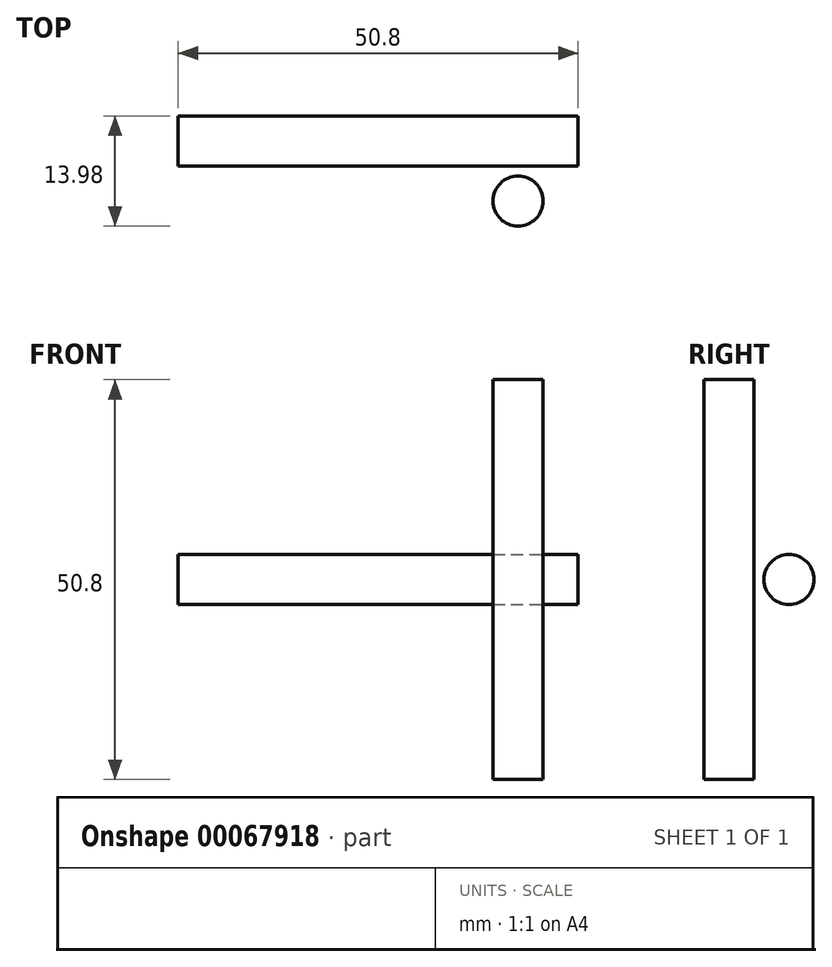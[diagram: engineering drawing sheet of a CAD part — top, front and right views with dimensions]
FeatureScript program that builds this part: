
annotation { "Feature Type Name" : "Feature", "Feature Type Description" : "" }
export const myFeature = defineFeature(function(context is Context, id is Id, definition is map)
    precondition{}
    {
        {
            assignVariable(context, id + "F0", {"name" : "ZPos", "anyValue" : 2});
        }
        {
            var Q0;
            Q0=qCreatedBy(makeId("Top.planeOp"),FACE);
            var sketch = newSketch(context, id + "F1", { "sketchPlane" : qUnion([Q0])});
            skCircle(sketch, "E0.cCircle", {"center": v(0, 0) * mm, "radius": 152.4 * mm, "construction": true});
            skLineSegment(sketch, "E0.0", {"start": v(87.99, 152.4) * mm, "end": v(175.98, 0) * mm});
            skLineSegment(sketch, "E0.1", {"start": v(175.98, 0) * mm, "end": v(87.99, -152.4) * mm});
            skLineSegment(sketch, "E0.2", {"start": v(87.99, -152.4) * mm, "end": v(-87.99, -152.4) * mm});
            skLineSegment(sketch, "E0.3", {"start": v(-87.99, -152.4) * mm, "end": v(-175.98, 0) * mm});
            skLineSegment(sketch, "E0.4", {"start": v(-175.98, 0) * mm, "end": v(-87.99, 152.4) * mm});
            skLineSegment(sketch, "E0.5", {"start": v(-87.99, 152.4) * mm, "end": v(87.99, 152.4) * mm});
            skPoint(sketch, "E0.0.midPoint", {"position": v(131.98, 76.2) * mm});
            skText(sketch, "E1", { "text": "1\n", "fontName": "OpenSans-Regular.ttf"});
            skText(sketch, "E2", { "text": "2\n", "fontName": "OpenSans-Regular.ttf"});
            skText(sketch, "E3", { "text": "3\n", "fontName": "OpenSans-Regular.ttf"});
            const initialGuessF1  = {"E1": [-0.00997, -0.1984, 1, 0, 0.02637], "E2": [0.15081, 0.07402, 1, 0, 0.02748], "E3": [-0.18048, 0.09683, 1, 0, 0.028]};
            skSetInitialGuess(sketch, initialGuessF1);
            skSolve(sketch);
        }
        {
            var Q0;
            Q0=makeQuery(id+"F1.imprint","IMPRINT",FACE,{"disambiguationData":[TD([[makeQuery(id+"F1.imprint","IMPRINT",EDGE,{"derivedFrom":sQuery(id+"F1.wireOp",EDGE,"E0.0")}),-1.0]])]});
            cPlane(context, id + "F2", {"entities" : qUnion([Q0]), "cplaneType" : CPlaneType.OFFSET, "offset" : (getVariable(context, 'ZPos')) * mm, "width" : 152.4 * mm, "height" : 152.4 * mm});
        }
        {
            var Q0;
            Q0=qCreatedBy(id+"F2.planeOp",FACE);
            var sketch = newSketch(context, id + "F3", { "sketchPlane" : qUnion([Q0])});
            skCircle(sketch, "E4.cCircle", {"center": v(-127, 127) * mm, "radius": 14.66 * mm, "construction": true});
            skLineSegment(sketch, "E4.0", {"start": v(-127, 156.33) * mm, "end": v(-101.6, 112.34) * mm});
            skLineSegment(sketch, "E4.1", {"start": v(-101.6, 112.34) * mm, "end": v(-152.4, 112.34) * mm});
            skLineSegment(sketch, "E4.2", {"start": v(-152.4, 112.34) * mm, "end": v(-127, 156.33) * mm});
            skPoint(sketch, "E4.0.midPoint", {"position": v(-114.3, 134.33) * mm});
            skSolve(sketch);
        }
        {
            var Q0;
            Q0=makeQuery(id+"F1.imprint","IMPRINT",FACE,{"disambiguationData":[TD([[makeQuery(id+"F1.imprint","IMPRINT",EDGE,{"derivedFrom":sQuery(id+"F1.wireOp",EDGE,"E0.0")}),-1.0]])]});
            var sketch = newSketch(context, id + "F4", { "sketchPlane" : qUnion([Q0])});
            skLineSegment(sketch, "E5", {"start": v(-25.4, -139.7) * mm, "end": v(25.4, -139.7) * mm});
            skLineSegment(sketch, "E6.1.0", {"start": v(133.68, 47.85) * mm, "end": v(108.28, 91.85) * mm});
            skLineSegment(sketch, "E6.2.0", {"start": v(-108.28, 91.85) * mm, "end": v(-133.68, 47.85) * mm});
            skPoint(sketch, "E6.center", {"position": v(0, 0) * mm});
            skSolve(sketch);
        }
        {
            var Q0;
            Q0=sQuery(id+"F3.wireOp",VERTEX,"E4.2.start");
            var Q1;
            Q1=sQuery(id+"F4.wireOp",VERTEX,"E5.start");
            var Q2;
            Q2=sQuery(id+"F4.wireOp",VERTEX,"E5.end");
            cPlane(context, id + "F5", {"entities" : qUnion([Q0, Q1, Q2]), "cplaneType" : CPlaneType.THREE_POINT, "offset" : 0 * mm, "width" : 152.4 * mm, "height" : 152.4 * mm});
        }
        {
            var Q0;
            Q0=qCreatedBy(id+"F5.planeOp",FACE);
            var sketch = newSketch(context, id + "F6", { "sketchPlane" : qUnion([Q0])});
            skLineSegment(sketch, "E7.0", {"start": v(-25.4, 136.95) * mm, "end": v(25.4, 136.95) * mm});
            skCircle(sketch, "E8", {"center": v(20.52, 132.07) * mm, "radius": 4.87 * mm});
            skLineSegment(sketch, "E9.0", {"start": v(-101.6, -120.16) * mm, "end": v(-152.4, -120.16) * mm});
            skLineSegment(sketch, "E10", {"start": v(-101.6, -120.16) * mm, "end": v(24.87, 129.87) * mm});
            skSolve(sketch);
        }
        {
            var Q0;
            Q0=sQuery(id+"F4.wireOp",VERTEX,"E6.1.0.start");
            var Q1;
            Q1=sQuery(id+"F4.wireOp",VERTEX,"E6.1.0.end");
            var Q2;
            Q2=sQuery(id+"F6.wireOp",VERTEX,"E10.start");
            cPlane(context, id + "F7", {"entities" : qUnion([Q0, Q1, Q2]), "cplaneType" : CPlaneType.THREE_POINT, "offset" : 25.4 * mm, "width" : 152.4 * mm, "height" : 152.4 * mm});
        }
        {
            var Q0;
            Q0=qCreatedBy(id+"F7.planeOp",FACE);
            var sketch = newSketch(context, id + "F8", { "sketchPlane" : qUnion([Q0])});
            skLineSegment(sketch, "E11.0", {"start": v(-141.1, -147.2) * mm, "end": v(-114.89, -103.68) * mm});
            skLineSegment(sketch, "E11.1", {"start": v(127.85, -47.34) * mm, "end": v(101.65, -90.86) * mm});
            skCircle(sketch, "E12", {"center": v(99.99, -84.17) * mm, "radius": 4.88 * mm});
            skLineSegment(sketch, "E13", {"start": v(101.65, -90.86) * mm, "end": v(100.15, -89.96) * mm, "construction": true});
            skLineSegment(sketch, "E14", {"start": v(-141.1, -147.2) * mm, "end": v(101.13, -88.9) * mm});
            skSolve(sketch);
        }
        {
            var Q0;
            Q0=sQuery(id+"F8.wireOp",VERTEX,"E14.start");
            var Q1;
            Q1=sQuery(id+"F4.wireOp",VERTEX,"E6.2.0.start");
            var Q2;
            Q2=sQuery(id+"F4.wireOp",VERTEX,"E6.2.0.end");
            cPlane(context, id + "F9", {"entities" : qUnion([Q0, Q1, Q2]), "cplaneType" : CPlaneType.THREE_POINT, "offset" : 25.4 * mm, "width" : 152.4 * mm, "height" : 152.4 * mm});
        }
        {
            var Q0;
            Q0=sQuery(id+"F4.wireOp",VERTEX,"E5.end");
            var Q1;
            Q1=sQuery(id+"F4.wireOp",EDGE,"E5");
            cPlane(context, id + "F10", {"entities" : qUnion([Q0, Q1]), "cplaneType" : CPlaneType.LINE_POINT, "offset" : 25.4 * mm, "width" : 152.4 * mm, "height" : 152.4 * mm});
        }
        {
            var Q0;
            Q0=qCreatedBy(id+"F10.planeOp",FACE);
            var sketch = newSketch(context, id + "F11", { "sketchPlane" : qUnion([Q0])});
            skCircle(sketch, "E15", {"center": v(-139.7, 0) * mm, "radius": 3.18 * mm});
            skSolve(sketch);
        }
        {
            var Q0;
            Q0=makeQuery(id+"F11.imprint","IMPRINT",FACE,{"disambiguationData":[TD([[makeQuery(id+"F11.imprint","IMPRINT",EDGE,{"derivedFrom":sQuery(id+"F11.wireOp",EDGE,"E15")}),1.0]])]});
            extrude(context, id + "F12", {"entities" : qUnion([Q0]), "oppositeDirection" : true, "depth" : 50.8 * mm});
        }
        {
            var Q0;
            Q0=makeQuery(id+"F1.imprint","IMPRINT",FACE,{"disambiguationData":[TD([[makeQuery(id+"F1.imprint","IMPRINT",EDGE,{"derivedFrom":sQuery(id+"F1.wireOp",EDGE,"E0.0")}),-1.0]])]});
            var sketch = newSketch(context, id + "F13", { "sketchPlane" : qUnion([Q0])});
            skCircle(sketch, "E16", {"center": v(17.78, -147.32) * mm, "radius": 3.18 * mm});
            skSolve(sketch);
        }
        {
            var Q0;
            Q0=makeQuery(id+"F13.imprint","IMPRINT",FACE,{"disambiguationData":[TD([[makeQuery(id+"F13.imprint","IMPRINT",EDGE,{"derivedFrom":sQuery(id+"F13.wireOp",EDGE,"E16")}),1.0]])]});
            extrude(context, id + "F14", {"entities" : qUnion([Q0]), "depth" : 25.4 * mm, "hasSecondDirection" : true, "secondDirectionOppositeDirection" : true, "secondDirectionDepth" : 25.4 * mm});
        }
    });
